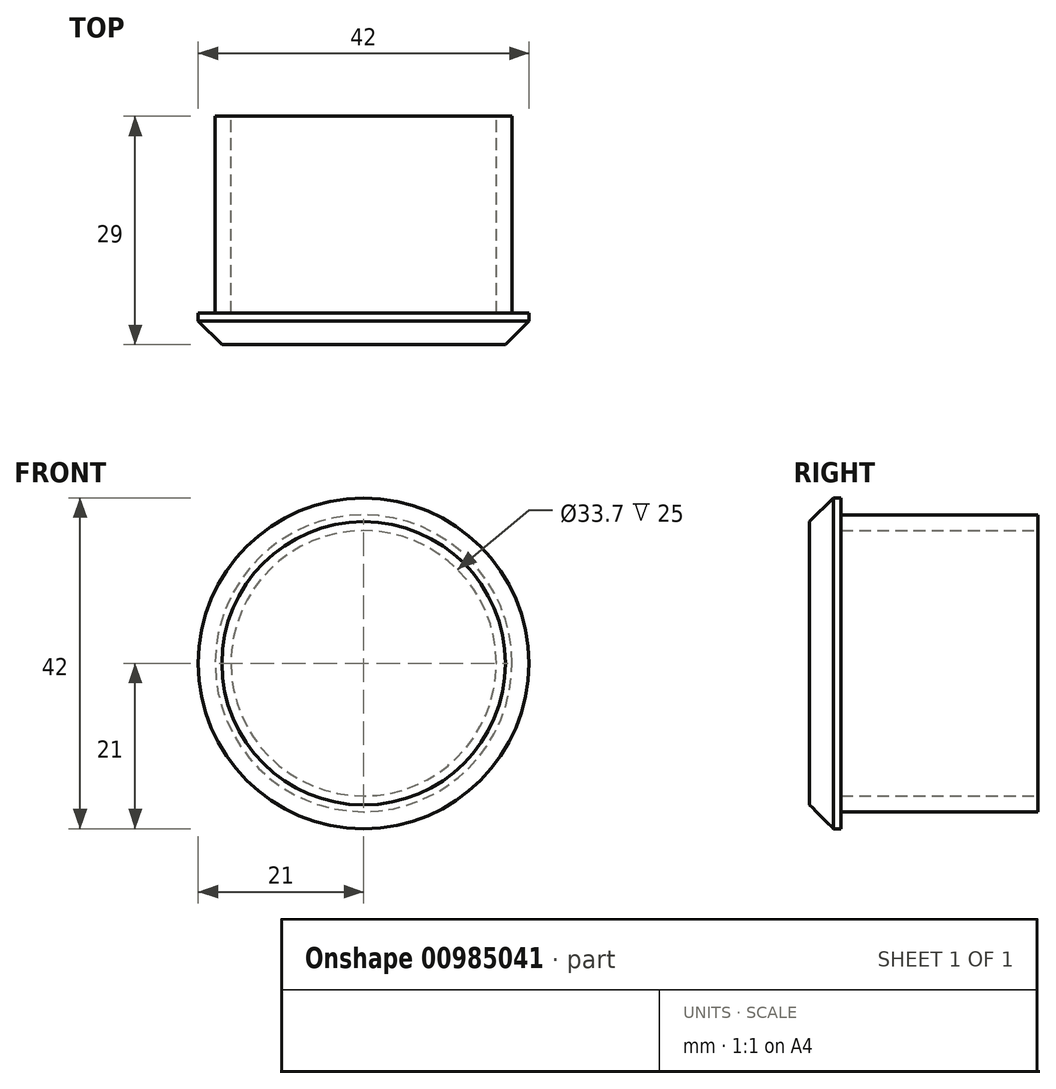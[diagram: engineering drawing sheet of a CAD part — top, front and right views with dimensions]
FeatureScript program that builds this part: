
annotation { "Feature Type Name" : "Feature", "Feature Type Description" : "" }
export const myFeature = defineFeature(function(context is Context, id is Id, definition is map)
    precondition{}
    {
        {
            var Q0;
            Q0=qCreatedBy(makeId("Front.planeOp"),FACE);
            var sketch = newSketch(context, id + "F0", { "sketchPlane" : qUnion([Q0])});
            skCircle(sketch, "E0", {"center": v(0, 0) * mm, "radius": 18.85 * mm});
            skCircle(sketch, "E1", {"center": v(0, 0) * mm, "radius": 16.85 * mm});
            skSolve(sketch);
        }
        {
            var Q0;
            Q0=makeQuery(id+"F0.imprint","IMPRINT",FACE,{"disambiguationData":[TD([[makeQuery(id+"F0.imprint","IMPRINT",EDGE,{"derivedFrom":sQuery(id+"F0.wireOp",EDGE,"E0")}),1.0]])]});
            extrude(context, id + "F1", {"entities" : qUnion([Q0]), "depth" : 25 * mm, "offsetDistance" : 25 * mm});
        }
        {
            var Q0;
            Q0=makeQuery(id+"F1.opExtrude","CAP_FACE",FACE,{"disambiguationData":[OSD([sQuery(id+"F0.wireOp",EDGE,"E0"),sQuery(id+"F0.wireOp",EDGE,"E1")])],"isStart":false});
            var sketch = newSketch(context, id + "F2", { "sketchPlane" : qUnion([Q0])});
            skCircle(sketch, "E2", {"center": v(0, 0) * mm, "radius": 21 * mm});
            skSolve(sketch);
        }
        {
            var Q0;
            Q0 = qSketchRegion(id + "F2", true);
            extrude(context, id + "F3", {"entities" : qUnion([Q0]), "operationType" : NewBodyOperationType.ADD, "depth" : 4 * mm, "offsetDistance" : 25 * mm});
        }
        {
            var Q0;
            Q0=makeQuery(id+"F3.opExtrude","CAP_EDGE",EDGE,{"disambiguationData":[OSD([sQuery(id+"F2.wireOp",EDGE,"E2")])],"isStart":false});
            chamfer(context, id + "F4", {"entities" : qUnion([Q0]), "width" : 3 * mm, "tangentPropagation" : true});
        }
    });
